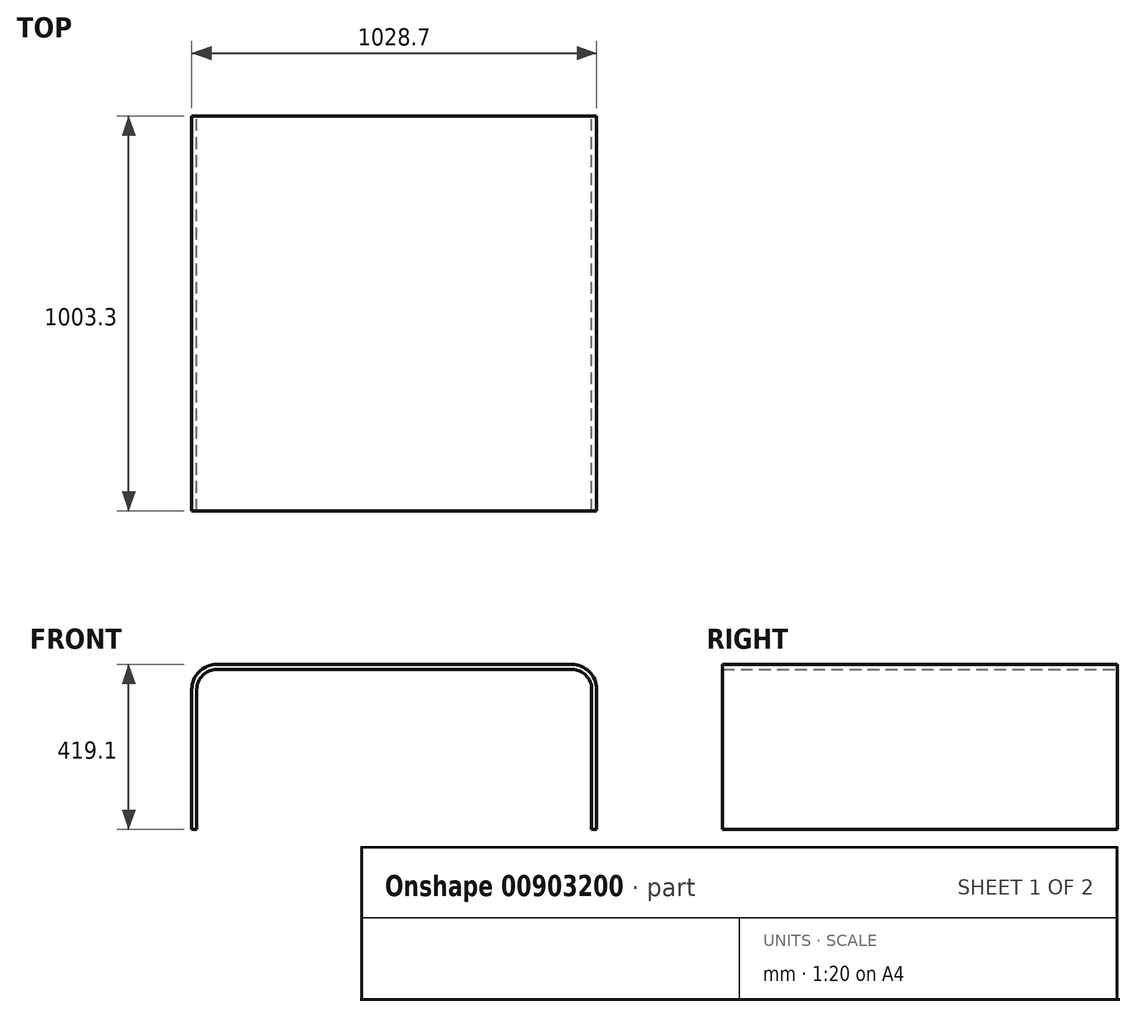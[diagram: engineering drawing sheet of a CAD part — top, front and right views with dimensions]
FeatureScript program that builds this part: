
annotation { "Feature Type Name" : "Feature", "Feature Type Description" : "" }
export const myFeature = defineFeature(function(context is Context, id is Id, definition is map)
    precondition{}
    {
        {
            var Q0;
            Q0=qCreatedBy(makeId("Front.planeOp"),FACE);
            var sketch = newSketch(context, id + "F0", { "sketchPlane" : qUnion([Q0])});
            skLineSegment(sketch, "E0", {"start": v(-501.65, 0) * mm, "end": v(-501.65, 355.6) * mm});
            skLineSegment(sketch, "E1", {"start": v(-450.85, 406.4) * mm, "end": v(450.85, 406.4) * mm});
            skLineSegment(sketch, "E2", {"start": v(501.65, 355.6) * mm, "end": v(501.65, 0) * mm});
            skLineSegment(sketch, "E3", {"start": v(0, 0) * mm, "end": v(0, 406.4) * mm, "construction": true});
            skPoint(sketch, "E4.visualSharp", {"position": v(-501.65, 406.4) * mm});
            skArc(sketch, "E4.filletArc", {"start": v(-450.85, 406.4) * mm, "mid": v(-486.77, 391.52) * mm, "end": v(-501.65, 355.6) * mm});
            skPoint(sketch, "E5.visualSharp", {"position": v(501.65, 406.4) * mm});
            skArc(sketch, "E5.filletArc", {"start": v(501.65, 355.6) * mm, "mid": v(486.77, 391.52) * mm, "end": v(450.85, 406.4) * mm});
            skLineSegment(sketch, "E6.0", {"start": v(-514.35, 0) * mm, "end": v(-514.35, 355.6) * mm});
            skLineSegment(sketch, "E6.1", {"start": v(514.35, 355.6) * mm, "end": v(514.35, 0) * mm});
            skArc(sketch, "E6.2", {"start": v(514.35, 355.6) * mm, "mid": v(495.75, 400.5) * mm, "end": v(450.85, 419.1) * mm});
            skLineSegment(sketch, "E6.3", {"start": v(-450.85, 419.1) * mm, "end": v(450.85, 419.1) * mm});
            skArc(sketch, "E6.4", {"start": v(-450.85, 419.1) * mm, "mid": v(-495.75, 400.5) * mm, "end": v(-514.35, 355.6) * mm});
            skLineSegment(sketch, "E7", {"start": v(-514.35, 0) * mm, "end": v(-501.65, 0) * mm});
            skLineSegment(sketch, "E8", {"start": v(501.65, 0) * mm, "end": v(514.35, 0) * mm});
            skSolve(sketch);
        }
        {
            var Q0;
            Q0 = qSketchRegion(id + "F0", true);
            extrude(context, id + "F1", {"entities" : qUnion([Q0]), "depth" : 1003.3 * mm, "offsetDistance" : 25.4 * mm});
        }
    });
